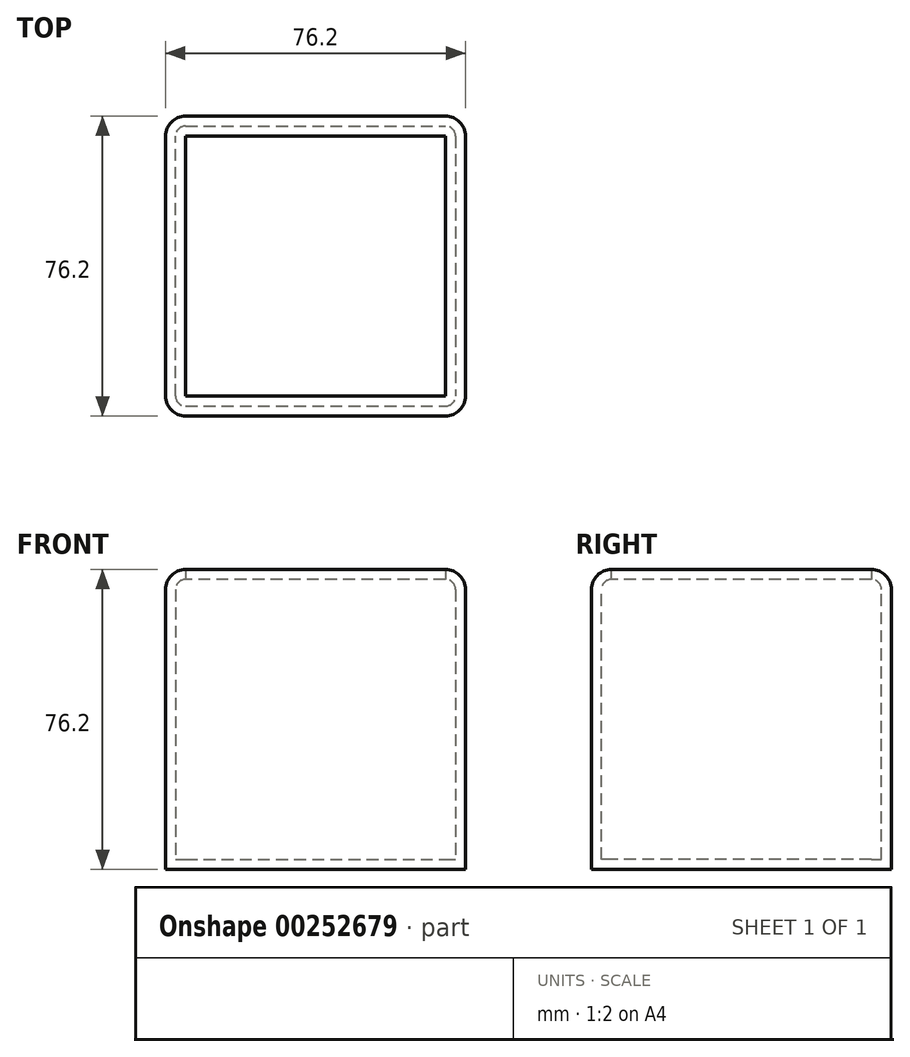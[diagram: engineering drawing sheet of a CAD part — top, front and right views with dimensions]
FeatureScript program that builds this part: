
annotation { "Feature Type Name" : "Feature", "Feature Type Description" : "" }
export const myFeature = defineFeature(function(context is Context, id is Id, definition is map)
    precondition{}
    {
        {
            var Q0;
            Q0=qCreatedBy(makeId("Top.planeOp"),FACE);
            var sketch = newSketch(context, id + "F0", { "sketchPlane" : qUnion([Q0])});
            skLineSegment(sketch, "E0.bottom", {"start": v(-30.33, 40.88) * mm, "end": v(45.87, 40.88) * mm});
            skLineSegment(sketch, "E0.top", {"start": v(-30.33, -35.32) * mm, "end": v(45.87, -35.32) * mm});
            skLineSegment(sketch, "E0.left", {"start": v(-30.33, 40.88) * mm, "end": v(-30.33, -35.32) * mm});
            skLineSegment(sketch, "E0.right", {"start": v(45.87, 40.88) * mm, "end": v(45.87, -35.32) * mm});
            skSolve(sketch);
        }
        {
            var Q0;
            Q0 = qSketchRegion(id + "F0", true);
            extrude(context, id + "F1", {"entities" : qUnion([Q0]), "depth" : 76.2 * mm});
        }
        {
            var Q0;
            Q0=makeQuery(id+"F1.opExtrude","CAP_EDGE",EDGE,{"disambiguationData":[OSD([sQuery(id+"F0.wireOp",EDGE,"E0.top")])],"isStart":false});
            var Q1;
            Q1=makeQuery(id+"F1.opExtrude","CAP_EDGE",EDGE,{"disambiguationData":[OSD([sQuery(id+"F0.wireOp",EDGE,"E0.right")])],"isStart":false});
            var Q2;
            Q2=makeQuery(id+"F1.opExtrude","CAP_EDGE",EDGE,{"disambiguationData":[OSD([sQuery(id+"F0.wireOp",EDGE,"E0.bottom")])],"isStart":false});
            var Q3;
            Q3=makeQuery(id+"F1.opExtrude","CAP_EDGE",EDGE,{"disambiguationData":[OSD([sQuery(id+"F0.wireOp",EDGE,"E0.left")])],"isStart":false});
            var Q4;
            Q4=makeQuery(id+"F1.opExtrude","SWEPT_EDGE",EDGE,{"disambiguationData":[OSD([sQuery(id+"F0.wireOp",EDGE,"E0.top"),sQuery(id+"F0.wireOp",EDGE,"E0.right")])]});
            var Q5;
            Q5=makeQuery(id+"F1.opExtrude","SWEPT_EDGE",EDGE,{"disambiguationData":[OSD([sQuery(id+"F0.wireOp",EDGE,"E0.top"),sQuery(id+"F0.wireOp",EDGE,"E0.left")])]});
            var Q6;
            Q6=makeQuery(id+"F1.opExtrude","SWEPT_EDGE",EDGE,{"disambiguationData":[OSD([sQuery(id+"F0.wireOp",EDGE,"E0.bottom"),sQuery(id+"F0.wireOp",EDGE,"E0.right")])]});
            var Q7;
            Q7=makeQuery(id+"F1.opExtrude","SWEPT_EDGE",EDGE,{"disambiguationData":[OSD([sQuery(id+"F0.wireOp",EDGE,"E0.bottom"),sQuery(id+"F0.wireOp",EDGE,"E0.left")])]});
            fillet(context, id + "F2", {"entities" : qUnion([Q0, Q1, Q2, Q3, Q4, Q5, Q6, Q7]), "radius" : 5.08 * mm, "tangentPropagation" : true, "allowEdgeOverflow" : false});
        }
        {
            var Q0;
            Q0=makeQuery(id+"F1.opExtrude","CAP_FACE",FACE,{"disambiguationData":[OSD([sQuery(id+"F0.wireOp",EDGE,"E0.bottom"),sQuery(id+"F0.wireOp",EDGE,"E0.top"),sQuery(id+"F0.wireOp",EDGE,"E0.left"),sQuery(id+"F0.wireOp",EDGE,"E0.right")])],"isStart":false});
            shell(context, id + "F3", {"entities" : qUnion([Q0]), "thickness" : 2.54 * mm});
        }
    });
